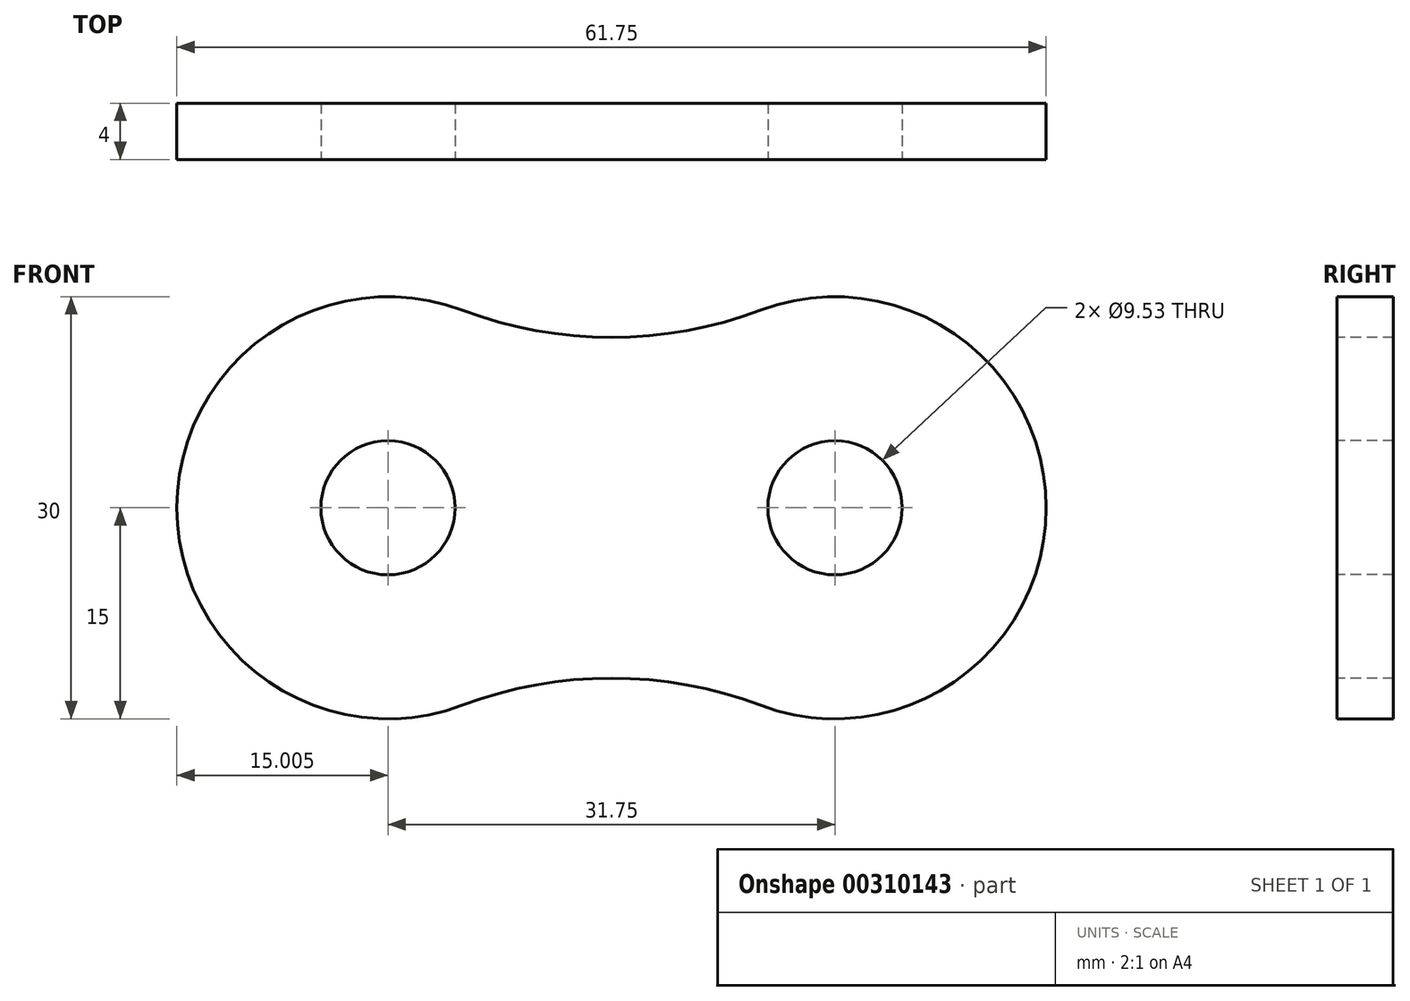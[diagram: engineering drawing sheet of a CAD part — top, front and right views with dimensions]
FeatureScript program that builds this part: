
annotation { "Feature Type Name" : "Feature", "Feature Type Description" : "" }
export const myFeature = defineFeature(function(context is Context, id is Id, definition is map)
    precondition{}
    {
        {
            var Q0;
            Q0=qCreatedBy(makeId("Front.planeOp"),FACE);
            var sketch = newSketch(context, id + "F0", { "sketchPlane" : qUnion([Q0])});
            skCircle(sketch, "E0", {"center": v(-26.6, 0) * mm, "radius": 4.77 * mm});
            skLineSegment(sketch, "E1", {"start": v(-26.6, 0) * mm, "end": v(5.15, 0) * mm});
            skCircle(sketch, "E2", {"center": v(5.15, 0) * mm, "radius": 4.77 * mm});
            skArc(sketch, "E3", {"start": v(-21.3, 14.04) * mm, "mid": v(-41.6, 0) * mm, "end": v(-21.3, -14.04) * mm});
            skArc(sketch, "E4", {"start": v(-0.14, -14.04) * mm, "mid": v(20.15, 0) * mm, "end": v(-0.14, 14.04) * mm});
            skArc(sketch, "E5", {"start": v(-21.3, 14.04) * mm, "mid": v(-10.72, 12.1) * mm, "end": v(-0.14, 14.04) * mm});
            skArc(sketch, "E6", {"start": v(-0.14, -14.04) * mm, "mid": v(-10.72, -12.1) * mm, "end": v(-21.3, -14.04) * mm});
            skSolve(sketch);
        }
        {
            var Q0;
            Q0=makeQuery(id+"F0.imprint","IMPRINT",FACE,{"disambiguationData":[TD([[makeQuery(id+"F0.imprint","IMPRINT",EDGE,{"derivedFrom":sQuery(id+"F0.wireOp",EDGE,"E0")}),-1.0]])]});
            extrude(context, id + "F1", {"entities" : qUnion([Q0]), "oppositeDirection" : true, "depth" : 4 * mm});
        }
    });
